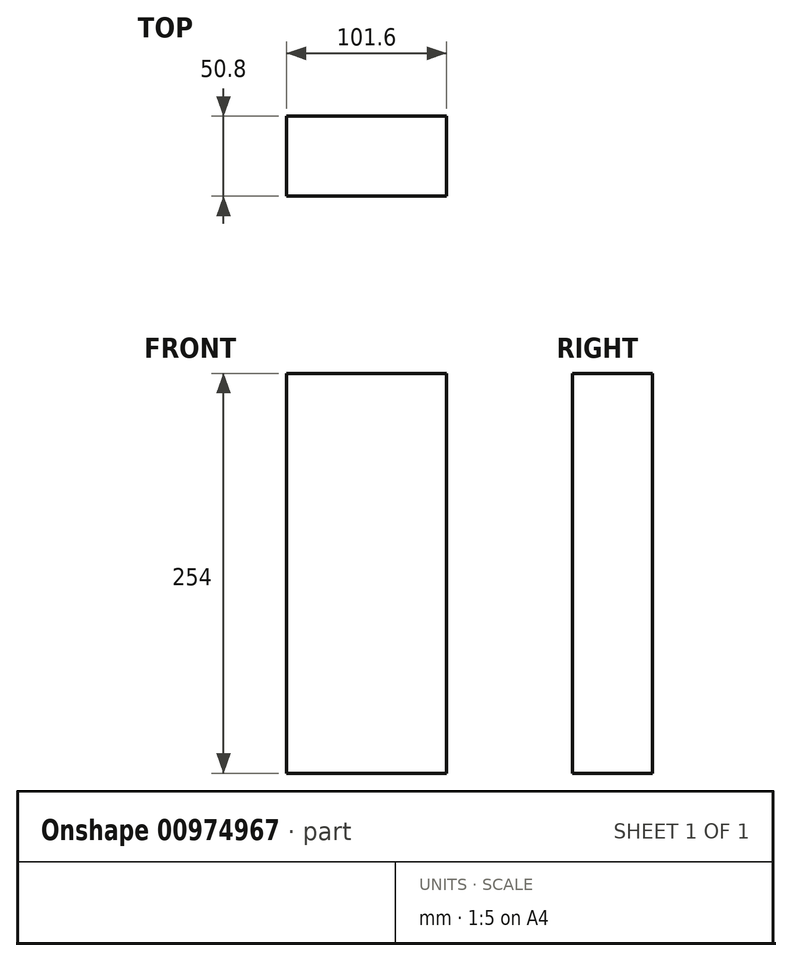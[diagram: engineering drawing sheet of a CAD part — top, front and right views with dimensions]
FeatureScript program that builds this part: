
annotation { "Feature Type Name" : "Feature", "Feature Type Description" : "" }
export const myFeature = defineFeature(function(context is Context, id is Id, definition is map)
    precondition{}
    {
        {
            var Q0;
            Q0=qCreatedBy(makeId("Front.planeOp"),FACE);
            var sketch = newSketch(context, id + "F0", { "sketchPlane" : qUnion([Q0])});
            skLineSegment(sketch, "E0.bottom", {"start": v(-53.1, 93.16) * mm, "end": v(48.5, 93.16) * mm});
            skLineSegment(sketch, "E0.top", {"start": v(-53.1, -160.84) * mm, "end": v(48.5, -160.84) * mm});
            skLineSegment(sketch, "E0.left", {"start": v(-53.1, 93.16) * mm, "end": v(-53.1, -160.84) * mm});
            skLineSegment(sketch, "E0.right", {"start": v(48.5, 93.16) * mm, "end": v(48.5, -160.84) * mm});
            skSolve(sketch);
        }
        {
            var Q0;
            Q0=makeQuery(id+"F0.imprint","IMPRINT",FACE,{"disambiguationData":[TD([[makeQuery(id+"F0.imprint","IMPRINT",EDGE,{"derivedFrom":sQuery(id+"F0.wireOp",EDGE,"E0.bottom")}),-1.0]])]});
            extrude(context, id + "F1", {"entities" : qUnion([Q0]), "depth" : 50.8 * mm, "offsetDistance" : 25.4 * mm});
        }
    });
